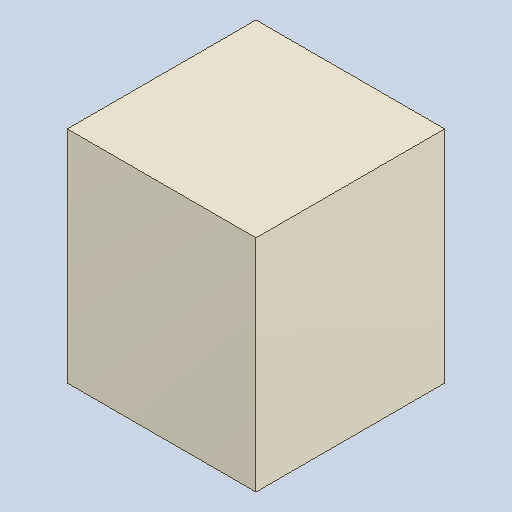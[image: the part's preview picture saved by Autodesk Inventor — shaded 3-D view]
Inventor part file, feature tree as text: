
AUTODESK INVENTOR PART (.ipt)
format: ipt  version: 2023.4 (Build 274418000, 418)  size: 82,944 bytes
history: native  units: mm
features: extrude x1
ambient origin geometry x8: Origin, YZ Plane, XZ Plane, XY Plane, X Axis, Y Axis, Z Axis, Center Point
bodies: Solid1 (feature_tree)
feature tree (1):
  extrude  "Extruded_23"  [1 undecoded]
note: 1 required parameter value undecoded (feature->parameter linkage not recoverable at this tier; creation-order binding heuristic only, values carry confidence <= 0.55)
